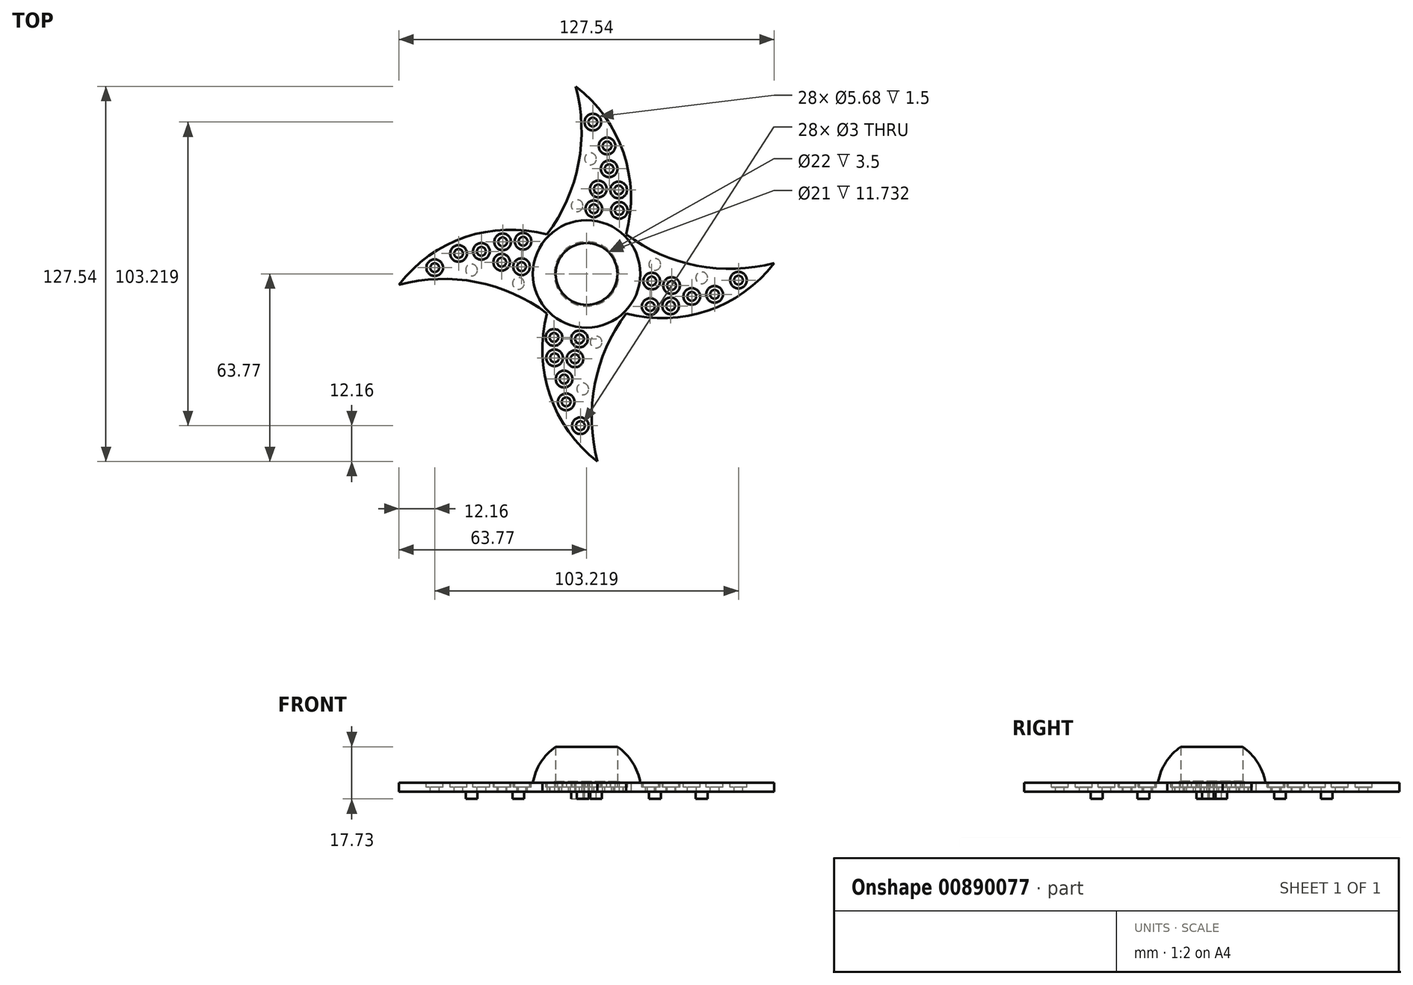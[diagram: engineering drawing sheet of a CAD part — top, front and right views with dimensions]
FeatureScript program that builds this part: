
annotation { "Feature Type Name" : "Feature", "Feature Type Description" : "" }
export const myFeature = defineFeature(function(context is Context, id is Id, definition is map)
    precondition{}
    {
        {
            var Q0;
            Q0=qCreatedBy(makeId("Top.planeOp"),FACE);
            var sketch = newSketch(context, id + "F0", { "sketchPlane" : qUnion([Q0])});
            skCircle(sketch, "E0", {"center": v(0, 0) * mm, "radius": 18.5 * mm});
            skLineSegment(sketch, "E1", {"start": v(0, 18.5) * mm, "end": v(0, -18.5) * mm});
            skSolve(sketch);
        }
        {
            var Q0;
            {var subQ0=sQuery(id+"F0.wireOp",EDGE,"E1");Q0=makeQuery(id+"F0.imprint","IMPRINT",FACE,{"disambiguationData":[TD([[makeQuery(id+"F0.imprint","IMPRINT",EDGE,{"derivedFrom":subQ0}),1.0]])]});}
            var Q1;
            Q1=sQuery(id+"F0.wireOp",EDGE,"E1");
            revolve(context, id + "F1", {"surfaceOperationType" : NewSurfaceOperationType.NEW, "entities" : qUnion([Q0]), "axis" : qUnion([Q1]), "revolveType" : RevolveType.ONE_DIRECTION, "angle" : 180 * degree});
        }
        {
            var Q0;
            Q0=makeQuery(id+"F1.opRevolve","CAP_FACE",FACE,{"disambiguationData":[OSD([sQuery(id+"F0.wireOp",EDGE,"E0"),sQuery(id+"F0.wireOp",EDGE,"E1")])],"isStart":true});
            var sketch = newSketch(context, id + "F2", { "sketchPlane" : qUnion([Q0])});
            skCircle(sketch, "E2", {"center": v(0, 0) * mm, "radius": 11 * mm});
            skSolve(sketch);
        }
        {
            var Q0;
            Q0=qSketchRegion(id+"F2",true);
            extrude(context, id + "F3", {"entities" : qUnion([Q0]), "operationType" : NewBodyOperationType.REMOVE, "oppositeDirection" : true, "depth" : 3.5 * mm, "offsetDistance" : 25 * mm});
        }
        {
            var Q0;
            Q0=makeQuery(id+"F3.boolean.opBoolean","COPY",FACE,{"derivedFrom":makeQuery(id+"F3.opExtrude","CAP_FACE",FACE,{"disambiguationData":[OSD([sQuery(id+"F2.wireOp",EDGE,"E2")])],"isStart":false})});
            var sketch = newSketch(context, id + "F4", { "sketchPlane" : qUnion([Q0])});
            skCircle(sketch, "E3", {"center": v(0, 0) * mm, "radius": 10.5 * mm});
            skSolve(sketch);
        }
        {
            var Q0;
            Q0=qSketchRegion(id+"F4",true);
            extrude(context, id + "F5", {"entities" : qUnion([Q0]), "operationType" : NewBodyOperationType.REMOVE, "surfaceOperationType" : NewSurfaceOperationType.ADD, "oppositeDirection" : true, "depth" : 25 * mm, "offsetDistance" : 25 * mm});
        }
        {
            var Q0;
            Q0=makeQuery(id+"F1.opRevolve","CAP_FACE",FACE,{"disambiguationData":[OSD([sQuery(id+"F0.wireOp",EDGE,"E0"),sQuery(id+"F0.wireOp",EDGE,"E1")])],"isStart":true});
            var sketch = newSketch(context, id + "F6", { "sketchPlane" : qUnion([Q0])});
            skCircle(sketch, "E4", {"center": v(0, 0) * mm, "radius": 17.5 * mm});
            skLineSegment(sketch, "E5", {"start": v(13.08, 13.08) * mm, "end": v(13.44, 13.44) * mm});
            skLineSegment(sketch, "E6", {"start": v(-13.08, 13.08) * mm, "end": v(-13.44, 13.44) * mm});
            skArc(sketch, "E7", {"start": v(3.7, 63.77) * mm, "mid": v(-12.5, 41.2) * mm, "end": v(-13.44, 13.44) * mm});
            skArc(sketch, "E8", {"start": v(3.7, 63.77) * mm, "mid": v(2.78, 37.48) * mm, "end": v(13.44, 13.44) * mm});
            skLineSegment(sketch, "E9.1.0", {"start": v(-13.08, -13.08) * mm, "end": v(-13.44, -13.44) * mm});
            skArc(sketch, "E9.1.1", {"start": v(-63.77, 3.7) * mm, "mid": v(-41.2, -12.5) * mm, "end": v(-13.44, -13.44) * mm});
            skArc(sketch, "E9.1.2", {"start": v(-63.77, 3.7) * mm, "mid": v(-37.48, 2.78) * mm, "end": v(-13.44, 13.44) * mm});
            skLineSegment(sketch, "E9.2.0", {"start": v(13.08, -13.08) * mm, "end": v(13.44, -13.44) * mm});
            skArc(sketch, "E9.2.1", {"start": v(-3.7, -63.77) * mm, "mid": v(12.5, -41.2) * mm, "end": v(13.44, -13.44) * mm});
            skArc(sketch, "E9.2.2", {"start": v(-3.7, -63.77) * mm, "mid": v(-2.78, -37.48) * mm, "end": v(-13.44, -13.44) * mm});
            skLineSegment(sketch, "E9.2.3", {"start": v(-13.08, -13.08) * mm, "end": v(-13.44, -13.44) * mm});
            skArc(sketch, "E9.3.1", {"start": v(63.77, -3.7) * mm, "mid": v(41.2, 12.5) * mm, "end": v(13.44, 13.44) * mm});
            skArc(sketch, "E9.3.2", {"start": v(63.77, -3.7) * mm, "mid": v(37.48, -2.78) * mm, "end": v(13.44, -13.44) * mm});
            skLineSegment(sketch, "E9.3.3", {"start": v(13.08, -13.08) * mm, "end": v(13.44, -13.44) * mm});
            skSolve(sketch);
        }
        {
            var Q0;
            Q0=qSketchRegion(id+"F6",true);
            extrude(context, id + "F7", {"entities" : qUnion([Q0]), "operationType" : NewBodyOperationType.ADD, "oppositeDirection" : true, "depth" : 3 * mm, "offsetDistance" : 25 * mm});
        }
        {
            var Q0;
            Q0=makeQuery(id+"F7.opExtrude","CAP_FACE",FACE,{"disambiguationData":[OSD([sQuery(id+"F6.wireOp",EDGE,"E4"),sQuery(id+"F6.wireOp",EDGE,"E7"),sQuery(id+"F6.wireOp",EDGE,"E8"),sQuery(id+"F6.wireOp",EDGE,"E9.1.1"),sQuery(id+"F6.wireOp",EDGE,"E9.1.2"),sQuery(id+"F6.wireOp",EDGE,"E9.2.1"),sQuery(id+"F6.wireOp",EDGE,"E9.2.2"),sQuery(id+"F6.wireOp",EDGE,"E9.3.1"),sQuery(id+"F6.wireOp",EDGE,"E9.3.2")])],"isStart":false});
            var sketch = newSketch(context, id + "F8", { "sketchPlane" : qUnion([Q0])});
            skCircle(sketch, "E10", {"center": v(-11.08, -21.6) * mm, "radius": 2.84 * mm});
            skCircle(sketch, "E11", {"center": v(-2.44, -22.11) * mm, "radius": 2.84 * mm});
            skCircle(sketch, "E12", {"center": v(-10.9, -28.54) * mm, "radius": 2.84 * mm});
            skCircle(sketch, "E13", {"center": v(-3.96, -28.88) * mm, "radius": 2.84 * mm});
            skCircle(sketch, "E14", {"center": v(-7.66, -35.75) * mm, "radius": 2.84 * mm});
            skCircle(sketch, "E15", {"center": v(-6.94, -43.5) * mm, "radius": 2.84 * mm});
            skCircle(sketch, "E16", {"center": v(-2.12, -51.6) * mm, "radius": 2.84 * mm});
            skCircle(sketch, "E17.1.0", {"center": v(21.6, -11.08) * mm, "radius": 2.84 * mm});
            skCircle(sketch, "E17.1.1", {"center": v(22.11, -2.44) * mm, "radius": 2.84 * mm});
            skCircle(sketch, "E17.1.2", {"center": v(28.54, -10.9) * mm, "radius": 2.84 * mm});
            skCircle(sketch, "E17.1.3", {"center": v(28.88, -3.96) * mm, "radius": 2.84 * mm});
            skCircle(sketch, "E17.1.4", {"center": v(35.75, -7.66) * mm, "radius": 2.84 * mm});
            skCircle(sketch, "E17.1.5", {"center": v(43.5, -6.94) * mm, "radius": 2.84 * mm});
            skCircle(sketch, "E17.1.6", {"center": v(51.6, -2.12) * mm, "radius": 2.84 * mm});
            skCircle(sketch, "E17.2.0", {"center": v(11.08, 21.6) * mm, "radius": 2.84 * mm});
            skCircle(sketch, "E17.2.1", {"center": v(2.44, 22.11) * mm, "radius": 2.84 * mm});
            skCircle(sketch, "E17.2.2", {"center": v(10.9, 28.54) * mm, "radius": 2.84 * mm});
            skCircle(sketch, "E17.2.3", {"center": v(3.96, 28.88) * mm, "radius": 2.84 * mm});
            skCircle(sketch, "E17.2.4", {"center": v(7.66, 35.75) * mm, "radius": 2.84 * mm});
            skCircle(sketch, "E17.2.5", {"center": v(6.94, 43.5) * mm, "radius": 2.84 * mm});
            skCircle(sketch, "E17.2.6", {"center": v(2.12, 51.6) * mm, "radius": 2.84 * mm});
            skCircle(sketch, "E17.3.0", {"center": v(-21.6, 11.08) * mm, "radius": 2.84 * mm});
            skCircle(sketch, "E17.3.1", {"center": v(-22.11, 2.44) * mm, "radius": 2.84 * mm});
            skCircle(sketch, "E17.3.2", {"center": v(-28.54, 10.9) * mm, "radius": 2.84 * mm});
            skCircle(sketch, "E17.3.3", {"center": v(-28.88, 3.96) * mm, "radius": 2.84 * mm});
            skCircle(sketch, "E17.3.4", {"center": v(-35.75, 7.66) * mm, "radius": 2.84 * mm});
            skCircle(sketch, "E17.3.5", {"center": v(-43.5, 6.94) * mm, "radius": 2.84 * mm});
            skCircle(sketch, "E17.3.6", {"center": v(-51.6, 2.12) * mm, "radius": 2.84 * mm});
            skPoint(sketch, "E17.center", {"position": v(0, 0) * mm});
            skSolve(sketch);
        }
        {
            var Q0;
            Q0=qSketchRegion(id+"F8",true);
            extrude(context, id + "F9", {"entities" : qUnion([Q0]), "operationType" : NewBodyOperationType.REMOVE, "oppositeDirection" : true, "depth" : 1.5 * mm, "offsetDistance" : 25 * mm});
        }
        {
            var Q0;
            Q0=makeQuery(id+"F7.opExtrude","CAP_FACE",FACE,{"disambiguationData":[OSD([sQuery(id+"F6.wireOp",EDGE,"E4"),sQuery(id+"F6.wireOp",EDGE,"E7"),sQuery(id+"F6.wireOp",EDGE,"E8"),sQuery(id+"F6.wireOp",EDGE,"E9.1.1"),sQuery(id+"F6.wireOp",EDGE,"E9.1.2"),sQuery(id+"F6.wireOp",EDGE,"E9.2.1"),sQuery(id+"F6.wireOp",EDGE,"E9.2.2"),sQuery(id+"F6.wireOp",EDGE,"E9.3.1"),sQuery(id+"F6.wireOp",EDGE,"E9.3.2")])],"isStart":false});
            var sketch = newSketch(context, id + "F10", { "sketchPlane" : qUnion([Q0])});
            skCircle(sketch, "E18", {"center": v(-2.44, -22.11) * mm, "radius": 1.5 * mm});
            skCircle(sketch, "E19", {"center": v(-22.11, 2.44) * mm, "radius": 1.5 * mm});
            skCircle(sketch, "E20", {"center": v(2.44, 22.11) * mm, "radius": 1.5 * mm});
            skCircle(sketch, "E21", {"center": v(22.11, -2.44) * mm, "radius": 1.5 * mm});
            skCircle(sketch, "E22", {"center": v(-11.08, -21.6) * mm, "radius": 1.5 * mm});
            skCircle(sketch, "E23", {"center": v(-10.9, -28.54) * mm, "radius": 1.5 * mm});
            skCircle(sketch, "E24", {"center": v(-3.96, -28.88) * mm, "radius": 1.5 * mm});
            skCircle(sketch, "E25", {"center": v(-7.66, -35.75) * mm, "radius": 1.5 * mm});
            skCircle(sketch, "E26", {"center": v(-6.94, -43.5) * mm, "radius": 1.5 * mm});
            skCircle(sketch, "E27", {"center": v(-2.12, -51.6) * mm, "radius": 1.5 * mm});
            skCircle(sketch, "E28.1.0", {"center": v(21.6, -11.08) * mm, "radius": 1.5 * mm});
            skCircle(sketch, "E28.1.1", {"center": v(28.54, -10.9) * mm, "radius": 1.5 * mm});
            skCircle(sketch, "E28.1.2", {"center": v(28.88, -3.96) * mm, "radius": 1.5 * mm});
            skCircle(sketch, "E28.1.4", {"center": v(35.75, -7.66) * mm, "radius": 1.5 * mm});
            skCircle(sketch, "E28.1.5", {"center": v(43.5, -6.94) * mm, "radius": 1.5 * mm});
            skCircle(sketch, "E28.1.6", {"center": v(51.6, -2.12) * mm, "radius": 1.5 * mm});
            skCircle(sketch, "E28.2.0", {"center": v(11.08, 21.6) * mm, "radius": 1.5 * mm});
            skCircle(sketch, "E28.2.1", {"center": v(10.9, 28.54) * mm, "radius": 1.5 * mm});
            skCircle(sketch, "E28.2.2", {"center": v(3.96, 28.88) * mm, "radius": 1.5 * mm});
            skCircle(sketch, "E28.2.4", {"center": v(7.66, 35.75) * mm, "radius": 1.5 * mm});
            skCircle(sketch, "E28.2.5", {"center": v(6.94, 43.5) * mm, "radius": 1.5 * mm});
            skCircle(sketch, "E28.2.6", {"center": v(2.12, 51.6) * mm, "radius": 1.5 * mm});
            skCircle(sketch, "E28.3.0", {"center": v(-21.6, 11.08) * mm, "radius": 1.5 * mm});
            skCircle(sketch, "E28.3.1", {"center": v(-28.54, 10.9) * mm, "radius": 1.5 * mm});
            skCircle(sketch, "E28.3.2", {"center": v(-28.88, 3.96) * mm, "radius": 1.5 * mm});
            skCircle(sketch, "E28.3.4", {"center": v(-35.75, 7.66) * mm, "radius": 1.5 * mm});
            skCircle(sketch, "E28.3.5", {"center": v(-43.5, 6.94) * mm, "radius": 1.5 * mm});
            skCircle(sketch, "E28.3.6", {"center": v(-51.6, 2.12) * mm, "radius": 1.5 * mm});
            skPoint(sketch, "E28.center", {"position": v(0, 0) * mm});
            skSolve(sketch);
        }
        {
            var Q0;
            Q0=qSketchRegion(id+"F10",true);
            extrude(context, id + "F11", {"entities" : qUnion([Q0]), "operationType" : NewBodyOperationType.REMOVE, "oppositeDirection" : true, "depth" : 25 * mm, "offsetDistance" : 25 * mm});
        }
        {
            var Q0;
            Q0=makeQuery(id+"F7.opExtrude","CAP_FACE",FACE,{"disambiguationData":[OSD([sQuery(id+"F6.wireOp",EDGE,"E4"),sQuery(id+"F6.wireOp",EDGE,"E7"),sQuery(id+"F6.wireOp",EDGE,"E8"),sQuery(id+"F6.wireOp",EDGE,"E9.1.1"),sQuery(id+"F6.wireOp",EDGE,"E9.1.2"),sQuery(id+"F6.wireOp",EDGE,"E9.2.1"),sQuery(id+"F6.wireOp",EDGE,"E9.2.2"),sQuery(id+"F6.wireOp",EDGE,"E9.3.1"),sQuery(id+"F6.wireOp",EDGE,"E9.3.2")])],"isStart":true});
            var sketch = newSketch(context, id + "F12", { "sketchPlane" : qUnion([Q0])});
            skCircle(sketch, "E29", {"center": v(-23.18, 3.23) * mm, "radius": 2 * mm});
            skCircle(sketch, "E30", {"center": v(-39.1, -1.31) * mm, "radius": 2 * mm});
            skCircle(sketch, "E31.1.0", {"center": v(-3.23, -23.18) * mm, "radius": 2 * mm});
            skCircle(sketch, "E31.1.1", {"center": v(1.31, -39.1) * mm, "radius": 2 * mm});
            skCircle(sketch, "E31.2.0", {"center": v(23.18, -3.23) * mm, "radius": 2 * mm});
            skCircle(sketch, "E31.2.1", {"center": v(39.1, 1.31) * mm, "radius": 2 * mm});
            skCircle(sketch, "E31.3.0", {"center": v(3.23, 23.18) * mm, "radius": 2 * mm});
            skCircle(sketch, "E31.3.1", {"center": v(-1.31, 39.1) * mm, "radius": 2 * mm});
            skPoint(sketch, "E31.center", {"position": v(0, 0) * mm});
            skSolve(sketch);
        }
        {
            var Q0;
            Q0=qSketchRegion(id+"F12",true);
            extrude(context, id + "F13", {"entities" : qUnion([Q0]), "operationType" : NewBodyOperationType.ADD, "depth" : 2.5 * mm, "offsetDistance" : 25 * mm});
        }
    });
